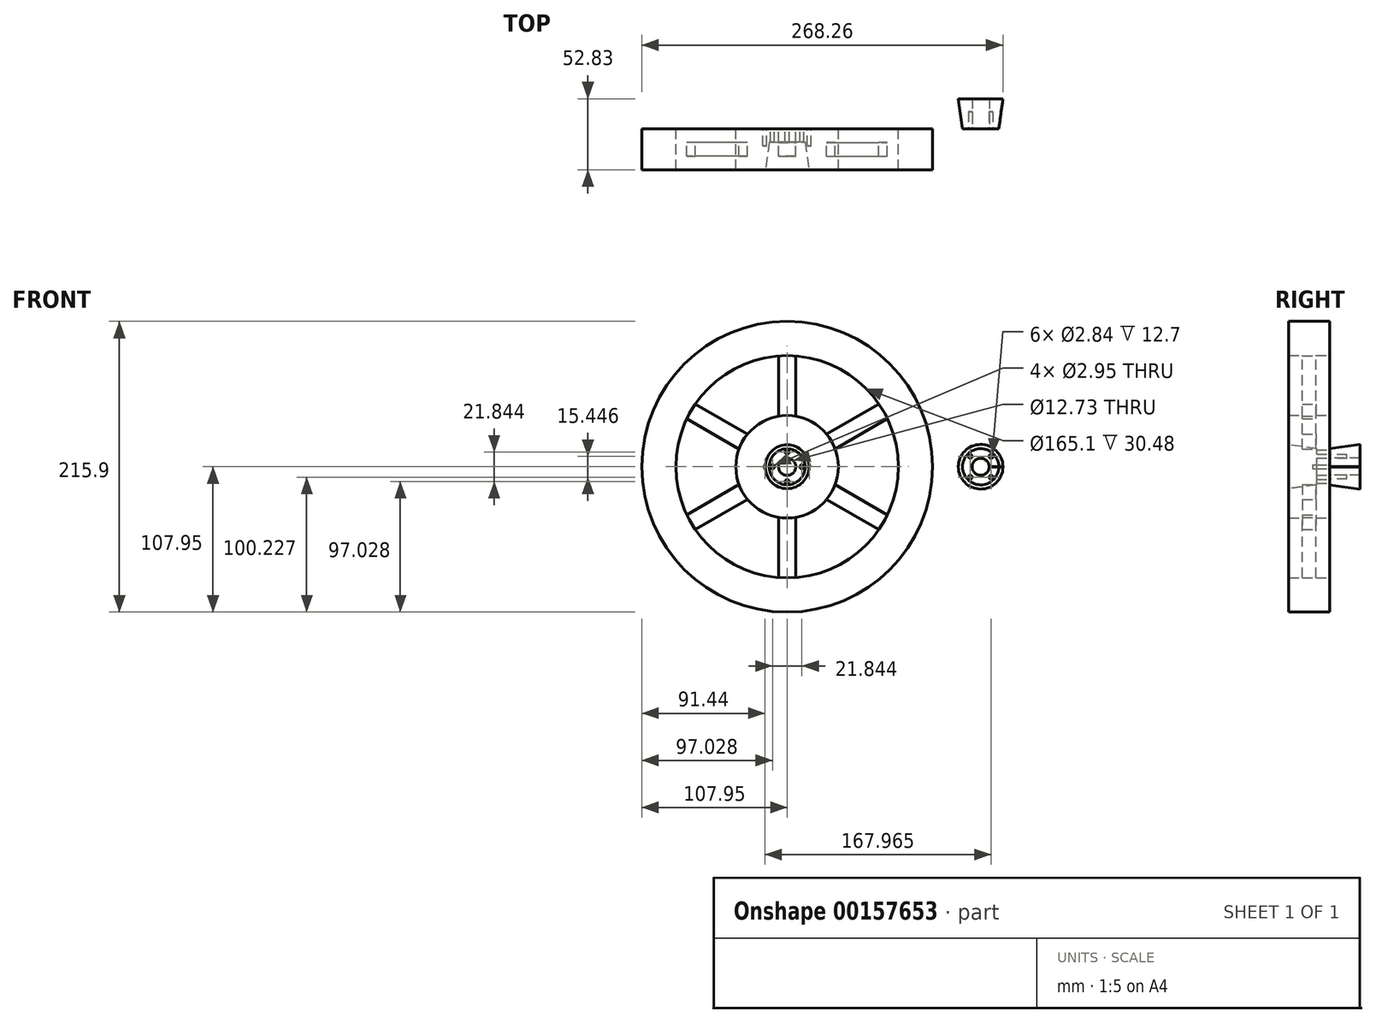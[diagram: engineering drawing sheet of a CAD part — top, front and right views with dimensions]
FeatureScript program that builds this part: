
annotation { "Feature Type Name" : "Feature", "Feature Type Description" : "" }
export const myFeature = defineFeature(function(context is Context, id is Id, definition is map)
    precondition{}
    {
        {
            var Q0;
            Q0=qCreatedBy(makeId("Front.planeOp"),FACE);
            var sketch = newSketch(context, id + "F0", { "sketchPlane" : qUnion([Q0])});
            skCircle(sketch, "E0", {"center": v(0, 0) * mm, "radius": 107.95 * mm});
            skArc(sketch, "E1", {"start": v(-74.45, 35.65) * mm, "mid": v(-82.55, 0) * mm, "end": v(-74.45, -35.65) * mm});
            skCircle(sketch, "E2", {"center": v(0, 0) * mm, "radius": 104.78 * mm});
            skArc(sketch, "E3", {"start": v(-35.7, 13.28) * mm, "mid": v(-38.1, 0) * mm, "end": v(-35.7, -13.28) * mm});
            skCircle(sketch, "E4", {"center": v(0, 0) * mm, "radius": 35.56 * mm});
            skCircle(sketch, "E5", {"center": v(0, 0) * mm, "radius": 6.36 * mm});
            skLineSegment(sketch, "E6", {"start": v(0, 0) * mm, "end": v(82.55, 0) * mm, "construction": true});
            skLineSegment(sketch, "E7", {"start": v(82.55, 0) * mm, "end": v(-82.55, 0) * mm, "construction": true});
            skLineSegment(sketch, "E8", {"start": v(0, 82.55) * mm, "end": v(0, -82.55) * mm, "construction": true});
            skLineSegment(sketch, "E9", {"start": v(-6.35, 65.1) * mm, "end": v(-6.35, 37.57) * mm});
            skLineSegment(sketch, "E10", {"start": v(-6.35, 37.57) * mm, "end": v(-6.35, 82.3) * mm});
            skLineSegment(sketch, "E11", {"start": v(6.35, 65.1) * mm, "end": v(6.35, 82.3) * mm});
            skLineSegment(sketch, "E12", {"start": v(6.35, 82.3) * mm, "end": v(6.35, 37.57) * mm});
            skLineSegment(sketch, "E13.1.0", {"start": v(-35.7, 13.28) * mm, "end": v(-74.45, 35.65) * mm});
            skLineSegment(sketch, "E13.1.1", {"start": v(-68.1, 46.65) * mm, "end": v(-29.36, 24.28) * mm});
            skLineSegment(sketch, "E13.2.0", {"start": v(-29.36, -24.28) * mm, "end": v(-68.1, -46.65) * mm});
            skLineSegment(sketch, "E13.2.1", {"start": v(-74.45, -35.65) * mm, "end": v(-35.7, -13.28) * mm});
            skLineSegment(sketch, "E13.3.0", {"start": v(6.35, -37.57) * mm, "end": v(6.35, -82.3) * mm});
            skLineSegment(sketch, "E13.3.1", {"start": v(-6.35, -82.3) * mm, "end": v(-6.35, -37.57) * mm});
            skLineSegment(sketch, "E13.4.0", {"start": v(35.7, -13.28) * mm, "end": v(74.45, -35.65) * mm});
            skLineSegment(sketch, "E13.4.1", {"start": v(68.1, -46.65) * mm, "end": v(29.36, -24.28) * mm});
            skLineSegment(sketch, "E13.5.0", {"start": v(29.36, 24.28) * mm, "end": v(68.1, 46.65) * mm});
            skLineSegment(sketch, "E13.5.1", {"start": v(74.45, 35.65) * mm, "end": v(35.7, 13.28) * mm});
            skArc(sketch, "E14.trimOffspring", {"start": v(-6.35, 82.3) * mm, "mid": v(-41.27, 71.5) * mm, "end": v(-68.1, 46.65) * mm});
            skArc(sketch, "E15.trimOffspring", {"start": v(-6.35, 37.57) * mm, "mid": v(-19.05, 33) * mm, "end": v(-29.36, 24.28) * mm});
            skArc(sketch, "E16.trimOffspring", {"start": v(68.1, 46.65) * mm, "mid": v(41.28, 71.5) * mm, "end": v(6.35, 82.3) * mm});
            skArc(sketch, "E17.trimOffspring", {"start": v(29.36, 24.28) * mm, "mid": v(19.05, 33) * mm, "end": v(6.35, 37.57) * mm});
            skArc(sketch, "E18.trimOffspring", {"start": v(74.45, -35.65) * mm, "mid": v(82.55, 0) * mm, "end": v(74.45, 35.65) * mm});
            skArc(sketch, "E19.trimOffspring", {"start": v(35.7, -13.28) * mm, "mid": v(38.1, 0) * mm, "end": v(35.7, 13.28) * mm});
            skArc(sketch, "E20.trimOffspring", {"start": v(-29.36, -24.28) * mm, "mid": v(-19.05, -33) * mm, "end": v(-6.35, -37.57) * mm});
            skArc(sketch, "E21.trimOffspring", {"start": v(-68.1, -46.65) * mm, "mid": v(-41.28, -71.5) * mm, "end": v(-6.35, -82.3) * mm});
            skArc(sketch, "E22.trimOffspring", {"start": v(6.35, -82.3) * mm, "mid": v(41.27, -71.5) * mm, "end": v(68.1, -46.65) * mm});
            skArc(sketch, "E23.trimOffspring", {"start": v(6.35, -37.57) * mm, "mid": v(19.05, -33) * mm, "end": v(29.36, -24.28) * mm});
            skSolve(sketch);
        }
        {
            var Q0;
            Q0=makeQuery(id+"F0.imprint","IMPRINT",FACE,{"disambiguationData":[TD([[makeQuery(id+"F0.imprint","IMPRINT",EDGE,{"derivedFrom":sQuery(id+"F0.wireOp",EDGE,"E1")}),-1.0]])]});
            var Q1;
            Q1=makeQuery(id+"F0.imprint","IMPRINT",FACE,{"disambiguationData":[TD([[makeQuery(id+"F0.imprint","IMPRINT",EDGE,{"derivedFrom":sQuery(id+"F0.wireOp",EDGE,"E0")}),1.0]])]});
            var Q2;
            Q2=makeQuery(id+"F0.imprint","IMPRINT",FACE,{"disambiguationData":[TD([[makeQuery(id+"F0.imprint","IMPRINT",EDGE,{"derivedFrom":sQuery(id+"F0.wireOp",EDGE,"E4")}),1.0]])]});
            extrude(context, id + "F1", {"entities" : qUnion([Q0, Q1, Q2]), "depth" : 30.48 * mm});
        }
        {
            var Q0;
            Q0=makeQuery(id+"F1.opExtrude","CAP_FACE",FACE,{"disambiguationData":[OSD([sQuery(id+"F0.wireOp",EDGE,"E0"),sQuery(id+"F0.wireOp",EDGE,"E1"),sQuery(id+"F0.wireOp",EDGE,"E3"),sQuery(id+"F0.wireOp",EDGE,"E5"),sQuery(id+"F0.wireOp",EDGE,"E10"),sQuery(id+"F0.wireOp",EDGE,"E12"),sQuery(id+"F0.wireOp",EDGE,"E13.1.0"),sQuery(id+"F0.wireOp",EDGE,"E13.1.1"),sQuery(id+"F0.wireOp",EDGE,"E13.2.0"),sQuery(id+"F0.wireOp",EDGE,"E13.2.1"),sQuery(id+"F0.wireOp",EDGE,"E13.3.0"),sQuery(id+"F0.wireOp",EDGE,"E13.3.1"),sQuery(id+"F0.wireOp",EDGE,"E13.4.0"),sQuery(id+"F0.wireOp",EDGE,"E13.4.1"),sQuery(id+"F0.wireOp",EDGE,"E13.5.0"),sQuery(id+"F0.wireOp",EDGE,"E13.5.1"),sQuery(id+"F0.wireOp",EDGE,"E14.trimOffspring"),sQuery(id+"F0.wireOp",EDGE,"E15.trimOffspring"),sQuery(id+"F0.wireOp",EDGE,"E16.trimOffspring"),sQuery(id+"F0.wireOp",EDGE,"E17.trimOffspring"),sQuery(id+"F0.wireOp",EDGE,"E18.trimOffspring"),sQuery(id+"F0.wireOp",EDGE,"E19.trimOffspring"),sQuery(id+"F0.wireOp",EDGE,"E20.trimOffspring"),sQuery(id+"F0.wireOp",EDGE,"E21.trimOffspring"),sQuery(id+"F0.wireOp",EDGE,"E22.trimOffspring"),sQuery(id+"F0.wireOp",EDGE,"E23.trimOffspring")])],"isStart":false});
            var sketch = newSketch(context, id + "F2", { "sketchPlane" : qUnion([Q0])});
            skCircle(sketch, "E24", {"center": v(0, 0) * mm, "radius": 82.55 * mm});
            skCircle(sketch, "E25", {"center": v(0, 0) * mm, "radius": 38.1 * mm});
            skSolve(sketch);
        }
        {
            var Q0;
            {var subQ2=makeQuery(id+"F1.opExtrude","CAP_EDGE",EDGE,{"disambiguationData":[OSD([sQuery(id+"F0.wireOp",EDGE,"E13.2.0")])],"isStart":false});Q0=makeQuery(id+"F2.imprint","IMPRINT",FACE,{"disambiguationData":[TD([[makeQuery(id+"F2.imprint","IMPRINT",EDGE,{"derivedFrom":subQ2}),-1.0]])]});}
            var Q1;
            {var subQ1=makeQuery(id+"F1.opExtrude","CAP_EDGE",EDGE,{"disambiguationData":[OSD([sQuery(id+"F0.wireOp",EDGE,"E13.3.0")])],"isStart":false});Q1=makeQuery(id+"F2.imprint","IMPRINT",FACE,{"disambiguationData":[TD([[makeQuery(id+"F2.imprint","IMPRINT",EDGE,{"derivedFrom":subQ1}),-1.0]])]});}
            var Q2;
            {var subQ1=makeQuery(id+"F1.opExtrude","CAP_EDGE",EDGE,{"disambiguationData":[OSD([sQuery(id+"F0.wireOp",EDGE,"E13.4.0")])],"isStart":false});Q2=makeQuery(id+"F2.imprint","IMPRINT",FACE,{"disambiguationData":[TD([[makeQuery(id+"F2.imprint","IMPRINT",EDGE,{"derivedFrom":subQ1}),-1.0]])]});}
            var Q3;
            {var subQ1=makeQuery(id+"F1.opExtrude","CAP_EDGE",EDGE,{"disambiguationData":[OSD([sQuery(id+"F0.wireOp",EDGE,"E13.5.0")])],"isStart":false});Q3=makeQuery(id+"F2.imprint","IMPRINT",FACE,{"disambiguationData":[TD([[makeQuery(id+"F2.imprint","IMPRINT",EDGE,{"derivedFrom":subQ1}),-1.0]])]});}
            var Q4;
            {var subQ1=makeQuery(id+"F1.opExtrude","CAP_EDGE",EDGE,{"disambiguationData":[OSD([sQuery(id+"F0.wireOp",EDGE,"E10")])],"isStart":false});Q4=makeQuery(id+"F2.imprint","IMPRINT",FACE,{"disambiguationData":[TD([[makeQuery(id+"F2.imprint","IMPRINT",EDGE,{"derivedFrom":subQ1}),-1.0]])]});}
            var Q5;
            {var subQ1=makeQuery(id+"F1.opExtrude","CAP_EDGE",EDGE,{"disambiguationData":[OSD([sQuery(id+"F0.wireOp",EDGE,"E13.1.0")])],"isStart":false});Q5=makeQuery(id+"F2.imprint","IMPRINT",FACE,{"disambiguationData":[TD([[makeQuery(id+"F2.imprint","IMPRINT",EDGE,{"derivedFrom":subQ1}),-1.0]])]});}
            extrude(context, id + "F3", {"entities" : qUnion([Q0, Q1, Q2, Q3, Q4, Q5]), "operationType" : NewBodyOperationType.REMOVE, "oppositeDirection" : true, "depth" : 10.16 * mm});
        }
        {
            var Q0;
            Q0=makeQuery(id+"F1.opExtrude","CAP_FACE",FACE,{"disambiguationData":[OSD([sQuery(id+"F0.wireOp",EDGE,"E0"),sQuery(id+"F0.wireOp",EDGE,"E1"),sQuery(id+"F0.wireOp",EDGE,"E3"),sQuery(id+"F0.wireOp",EDGE,"E5"),sQuery(id+"F0.wireOp",EDGE,"E10"),sQuery(id+"F0.wireOp",EDGE,"E12"),sQuery(id+"F0.wireOp",EDGE,"E13.1.0"),sQuery(id+"F0.wireOp",EDGE,"E13.1.1"),sQuery(id+"F0.wireOp",EDGE,"E13.2.0"),sQuery(id+"F0.wireOp",EDGE,"E13.2.1"),sQuery(id+"F0.wireOp",EDGE,"E13.3.0"),sQuery(id+"F0.wireOp",EDGE,"E13.3.1"),sQuery(id+"F0.wireOp",EDGE,"E13.4.0"),sQuery(id+"F0.wireOp",EDGE,"E13.4.1"),sQuery(id+"F0.wireOp",EDGE,"E13.5.0"),sQuery(id+"F0.wireOp",EDGE,"E13.5.1"),sQuery(id+"F0.wireOp",EDGE,"E14.trimOffspring"),sQuery(id+"F0.wireOp",EDGE,"E15.trimOffspring"),sQuery(id+"F0.wireOp",EDGE,"E16.trimOffspring"),sQuery(id+"F0.wireOp",EDGE,"E17.trimOffspring"),sQuery(id+"F0.wireOp",EDGE,"E18.trimOffspring"),sQuery(id+"F0.wireOp",EDGE,"E19.trimOffspring"),sQuery(id+"F0.wireOp",EDGE,"E20.trimOffspring"),sQuery(id+"F0.wireOp",EDGE,"E21.trimOffspring"),sQuery(id+"F0.wireOp",EDGE,"E22.trimOffspring"),sQuery(id+"F0.wireOp",EDGE,"E23.trimOffspring")])],"isStart":true});
            var sketch = newSketch(context, id + "F4", { "sketchPlane" : qUnion([Q0])});
            skCircle(sketch, "E26", {"center": v(0, 0) * mm, "radius": 82.55 * mm});
            skCircle(sketch, "E27", {"center": v(0, 0) * mm, "radius": 38.1 * mm});
            skSolve(sketch);
        }
        {
            var Q0;
            {var subQ2=makeQuery(id+"F1.opExtrude","CAP_EDGE",EDGE,{"disambiguationData":[OSD([sQuery(id+"F0.wireOp",EDGE,"E13.2.0")])],"isStart":true});Q0=makeQuery(id+"F4.imprint","IMPRINT",FACE,{"disambiguationData":[TD([[makeQuery(id+"F4.imprint","IMPRINT",EDGE,{"derivedFrom":subQ2}),1.0]])]});}
            var Q1;
            {var subQ1=makeQuery(id+"F1.opExtrude","CAP_EDGE",EDGE,{"disambiguationData":[OSD([sQuery(id+"F0.wireOp",EDGE,"E13.1.0")])],"isStart":true});Q1=makeQuery(id+"F4.imprint","IMPRINT",FACE,{"disambiguationData":[TD([[makeQuery(id+"F4.imprint","IMPRINT",EDGE,{"derivedFrom":subQ1}),1.0]])]});}
            var Q2;
            {var subQ1=makeQuery(id+"F1.opExtrude","CAP_EDGE",EDGE,{"disambiguationData":[OSD([sQuery(id+"F0.wireOp",EDGE,"E10")])],"isStart":true});Q2=makeQuery(id+"F4.imprint","IMPRINT",FACE,{"disambiguationData":[TD([[makeQuery(id+"F4.imprint","IMPRINT",EDGE,{"derivedFrom":subQ1}),1.0]])]});}
            var Q3;
            {var subQ1=makeQuery(id+"F1.opExtrude","CAP_EDGE",EDGE,{"disambiguationData":[OSD([sQuery(id+"F0.wireOp",EDGE,"E13.5.0")])],"isStart":true});Q3=makeQuery(id+"F4.imprint","IMPRINT",FACE,{"disambiguationData":[TD([[makeQuery(id+"F4.imprint","IMPRINT",EDGE,{"derivedFrom":subQ1}),1.0]])]});}
            var Q4;
            {var subQ1=makeQuery(id+"F1.opExtrude","CAP_EDGE",EDGE,{"disambiguationData":[OSD([sQuery(id+"F0.wireOp",EDGE,"E13.4.0")])],"isStart":true});Q4=makeQuery(id+"F4.imprint","IMPRINT",FACE,{"disambiguationData":[TD([[makeQuery(id+"F4.imprint","IMPRINT",EDGE,{"derivedFrom":subQ1}),1.0]])]});}
            var Q5;
            {var subQ1=makeQuery(id+"F1.opExtrude","CAP_EDGE",EDGE,{"disambiguationData":[OSD([sQuery(id+"F0.wireOp",EDGE,"E13.3.0")])],"isStart":true});Q5=makeQuery(id+"F4.imprint","IMPRINT",FACE,{"disambiguationData":[TD([[makeQuery(id+"F4.imprint","IMPRINT",EDGE,{"derivedFrom":subQ1}),1.0]])]});}
            extrude(context, id + "F5", {"entities" : qUnion([Q0, Q1, Q2, Q3, Q4, Q5]), "operationType" : NewBodyOperationType.REMOVE, "oppositeDirection" : true, "depth" : 10.16 * mm});
        }
        {
            var Q0;
            {var subQ1=sQuery(id+"F0.wireOp",EDGE,"E13.5.0");var subQ2=sQuery(id+"F0.wireOp",EDGE,"E13.5.1");var subQ3=sQuery(id+"F0.wireOp",EDGE,"E23.trimOffspring");var subQ4=sQuery(id+"F0.wireOp",EDGE,"E19.trimOffspring");var subQ5=sQuery(id+"F0.wireOp",EDGE,"E20.trimOffspring");var subQ6=sQuery(id+"F0.wireOp",EDGE,"E3");var subQ7=sQuery(id+"F0.wireOp",EDGE,"E13.1.0");var subQ8=sQuery(id+"F0.wireOp",EDGE,"E13.1.1");var subQ9=sQuery(id+"F0.wireOp",EDGE,"E17.trimOffspring");var subQ10=sQuery(id+"F0.wireOp",EDGE,"E5");var subQ11=sQuery(id+"F0.wireOp",EDGE,"E15.trimOffspring");var subQ12=sQuery(id+"F0.wireOp",EDGE,"E10");var subQ13=sQuery(id+"F0.wireOp",EDGE,"E12");var subQ14=sQuery(id+"F0.wireOp",EDGE,"E13.2.1");var subQ15=sQuery(id+"F0.wireOp",EDGE,"E13.2.0");var subQ16=sQuery(id+"F0.wireOp",EDGE,"E13.3.0");var subQ17=sQuery(id+"F0.wireOp",EDGE,"E13.3.1");var subQ18=sQuery(id+"F0.wireOp",EDGE,"E13.4.0");var subQ19=sQuery(id+"F0.wireOp",EDGE,"E13.4.1");Q0=makeQuery(id+"F3.boolean.opBoolean","SPLIT",FACE,{"disambiguationData":[TD([makeQuery(id+"F1.opExtrude","SWEPT_FACE",FACE,{"disambiguationData":[OSD([subQ6])]})])],"derivedFrom":makeQuery(id+"F1.opExtrude","CAP_FACE",FACE,{"disambiguationData":[OSD([sQuery(id+"F0.wireOp",EDGE,"E0"),sQuery(id+"F0.wireOp",EDGE,"E1"),subQ6,subQ10,subQ12,subQ13,subQ7,subQ8,subQ15,subQ14,subQ16,subQ17,subQ18,subQ19,subQ1,subQ2,sQuery(id+"F0.wireOp",EDGE,"E14.trimOffspring"),subQ11,sQuery(id+"F0.wireOp",EDGE,"E16.trimOffspring"),subQ9,sQuery(id+"F0.wireOp",EDGE,"E18.trimOffspring"),subQ4,subQ5,sQuery(id+"F0.wireOp",EDGE,"E21.trimOffspring"),sQuery(id+"F0.wireOp",EDGE,"E22.trimOffspring"),subQ3])],"isStart":false})});}
            var sketch = newSketch(context, id + "F6", { "sketchPlane" : qUnion([Q0])});
            skCircle(sketch, "E28", {"center": v(0, 0) * mm, "radius": 13.34 * mm});
            skSolve(sketch);
        }
        {
            var Q0;
            Q0=makeQuery(id+"F6.imprint","IMPRINT",FACE,{"disambiguationData":[TD([[makeQuery(id+"F6.imprint","IMPRINT",EDGE,{"derivedFrom":sQuery(id+"F6.wireOp",EDGE,"E28")}),1.0]])]});
            extrude(context, id + "F7", {"entities" : qUnion([Q0]), "operationType" : NewBodyOperationType.REMOVE, "oppositeDirection" : true, "depth" : 20.83 * mm});
        }
        {
            var Q0;
            Q0=makeQuery(id+"F7.boolean.opBoolean","COPY",FACE,{"derivedFrom":makeQuery(id+"F7.opExtrude","CAP_FACE",FACE,{"disambiguationData":[OSD([sQuery(id+"F0.wireOp",EDGE,"E5"),sQuery(id+"F6.wireOp",EDGE,"E28")])],"isStart":false})});
            extrude(context, id + "F8", {"entities" : qUnion([Q0]), "operationType" : NewBodyOperationType.REMOVE, "depth" : 25.4 * mm, "hasDraft" : true, "draftAngle" : 8 * degree});
        }
        {
            var Q0;
            {var subQ1=sQuery(id+"F0.wireOp",EDGE,"E13.5.0");var subQ2=sQuery(id+"F0.wireOp",EDGE,"E13.5.1");var subQ3=sQuery(id+"F0.wireOp",EDGE,"E23.trimOffspring");var subQ4=sQuery(id+"F0.wireOp",EDGE,"E19.trimOffspring");var subQ5=sQuery(id+"F0.wireOp",EDGE,"E20.trimOffspring");var subQ7=sQuery(id+"F0.wireOp",EDGE,"E13.1.0");var subQ8=sQuery(id+"F0.wireOp",EDGE,"E13.1.1");var subQ9=sQuery(id+"F0.wireOp",EDGE,"E3");var subQ10=sQuery(id+"F0.wireOp",EDGE,"E17.trimOffspring");var subQ11=sQuery(id+"F0.wireOp",EDGE,"E5");var subQ12=sQuery(id+"F0.wireOp",EDGE,"E10");var subQ13=sQuery(id+"F0.wireOp",EDGE,"E12");var subQ14=sQuery(id+"F0.wireOp",EDGE,"E15.trimOffspring");var subQ15=sQuery(id+"F0.wireOp",EDGE,"E13.2.1");var subQ16=sQuery(id+"F0.wireOp",EDGE,"E13.2.0");var subQ17=sQuery(id+"F0.wireOp",EDGE,"E13.4.0");var subQ18=sQuery(id+"F0.wireOp",EDGE,"E13.4.1");var subQ19=sQuery(id+"F0.wireOp",EDGE,"E13.3.0");var subQ20=sQuery(id+"F0.wireOp",EDGE,"E13.3.1");Q0=makeQuery(id+"F5.boolean.opBoolean","SPLIT",FACE,{"disambiguationData":[TD([makeQuery(id+"F1.opExtrude","SWEPT_FACE",FACE,{"disambiguationData":[OSD([subQ9])]})])],"derivedFrom":makeQuery(id+"F1.opExtrude","CAP_FACE",FACE,{"disambiguationData":[OSD([sQuery(id+"F0.wireOp",EDGE,"E0"),sQuery(id+"F0.wireOp",EDGE,"E1"),subQ9,subQ11,subQ12,subQ13,subQ7,subQ8,subQ16,subQ15,subQ19,subQ20,subQ17,subQ18,subQ1,subQ2,sQuery(id+"F0.wireOp",EDGE,"E14.trimOffspring"),subQ14,sQuery(id+"F0.wireOp",EDGE,"E16.trimOffspring"),subQ10,sQuery(id+"F0.wireOp",EDGE,"E18.trimOffspring"),subQ4,subQ5,sQuery(id+"F0.wireOp",EDGE,"E21.trimOffspring"),sQuery(id+"F0.wireOp",EDGE,"E22.trimOffspring"),subQ3])],"isStart":true})});}
            var sketch = newSketch(context, id + "F9", { "sketchPlane" : qUnion([Q0])});
            skCircle(sketch, "E29", {"center": v(0, 0) * mm, "radius": 10.92 * mm, "construction": true});
            skCircle(sketch, "E30", {"center": v(0, 10.92) * mm, "radius": 1.47 * mm});
            skCircle(sketch, "E31.1.0", {"center": v(-10.92, 0) * mm, "radius": 1.47 * mm});
            skCircle(sketch, "E31.2.0", {"center": v(0, -10.92) * mm, "radius": 1.47 * mm});
            skCircle(sketch, "E31.3.0", {"center": v(10.92, 0) * mm, "radius": 1.47 * mm});
            skSolve(sketch);
        }
        {
            var Q0;
            Q0=makeQuery(id+"F9.imprint","IMPRINT",FACE,{"disambiguationData":[TD([[makeQuery(id+"F9.imprint","IMPRINT",EDGE,{"derivedFrom":sQuery(id+"F9.wireOp",EDGE,"E31.1.0")}),1.0]])]});
            var Q1;
            Q1=makeQuery(id+"F9.imprint","IMPRINT",FACE,{"disambiguationData":[TD([[makeQuery(id+"F9.imprint","IMPRINT",EDGE,{"derivedFrom":sQuery(id+"F9.wireOp",EDGE,"E30")}),1.0]])]});
            var Q2;
            Q2=makeQuery(id+"F9.imprint","IMPRINT",FACE,{"disambiguationData":[TD([[makeQuery(id+"F9.imprint","IMPRINT",EDGE,{"derivedFrom":sQuery(id+"F9.wireOp",EDGE,"E31.2.0")}),1.0]])]});
            var Q3;
            Q3=makeQuery(id+"F9.imprint","IMPRINT",FACE,{"disambiguationData":[TD([[makeQuery(id+"F9.imprint","IMPRINT",EDGE,{"derivedFrom":sQuery(id+"F9.wireOp",EDGE,"E31.3.0")}),1.0]])]});
            extrude(context, id + "F10", {"entities" : qUnion([Q0, Q1, Q2, Q3]), "operationType" : NewBodyOperationType.REMOVE, "oppositeDirection" : true, "depth" : 25.4 * mm});
        }
        {
            var Q0;
            {var subQ1=sQuery(id+"F0.wireOp",EDGE,"E13.5.0");var subQ2=sQuery(id+"F0.wireOp",EDGE,"E13.5.1");var subQ3=sQuery(id+"F0.wireOp",EDGE,"E23.trimOffspring");var subQ4=sQuery(id+"F0.wireOp",EDGE,"E19.trimOffspring");var subQ5=sQuery(id+"F0.wireOp",EDGE,"E20.trimOffspring");var subQ7=sQuery(id+"F0.wireOp",EDGE,"E13.1.0");var subQ8=sQuery(id+"F0.wireOp",EDGE,"E13.1.1");var subQ9=sQuery(id+"F0.wireOp",EDGE,"E3");var subQ10=sQuery(id+"F0.wireOp",EDGE,"E17.trimOffspring");var subQ11=sQuery(id+"F0.wireOp",EDGE,"E5");var subQ12=sQuery(id+"F0.wireOp",EDGE,"E10");var subQ13=sQuery(id+"F0.wireOp",EDGE,"E12");var subQ14=sQuery(id+"F0.wireOp",EDGE,"E15.trimOffspring");var subQ15=sQuery(id+"F0.wireOp",EDGE,"E13.2.1");var subQ16=sQuery(id+"F0.wireOp",EDGE,"E13.2.0");var subQ17=sQuery(id+"F0.wireOp",EDGE,"E13.4.0");var subQ18=sQuery(id+"F0.wireOp",EDGE,"E13.4.1");var subQ19=sQuery(id+"F0.wireOp",EDGE,"E13.3.0");var subQ20=sQuery(id+"F0.wireOp",EDGE,"E13.3.1");Q0=makeQuery(id+"F5.boolean.opBoolean","SPLIT",FACE,{"disambiguationData":[TD([makeQuery(id+"F1.opExtrude","SWEPT_FACE",FACE,{"disambiguationData":[OSD([subQ9])]})])],"derivedFrom":makeQuery(id+"F1.opExtrude","CAP_FACE",FACE,{"disambiguationData":[OSD([sQuery(id+"F0.wireOp",EDGE,"E0"),sQuery(id+"F0.wireOp",EDGE,"E1"),subQ9,subQ11,subQ12,subQ13,subQ7,subQ8,subQ16,subQ15,subQ19,subQ20,subQ17,subQ18,subQ1,subQ2,sQuery(id+"F0.wireOp",EDGE,"E14.trimOffspring"),subQ14,sQuery(id+"F0.wireOp",EDGE,"E16.trimOffspring"),subQ10,sQuery(id+"F0.wireOp",EDGE,"E18.trimOffspring"),subQ4,subQ5,sQuery(id+"F0.wireOp",EDGE,"E21.trimOffspring"),sQuery(id+"F0.wireOp",EDGE,"E22.trimOffspring"),subQ3])],"isStart":true})});}
            var sketch = newSketch(context, id + "F11", { "sketchPlane" : qUnion([Q0])});
            skCircle(sketch, "E32", {"center": v(0, 0) * mm, "radius": 16.51 * mm, "construction": true});
            skCircle(sketch, "E33", {"center": v(16.51, 0) * mm, "radius": 1.42 * mm});
            skCircle(sketch, "E34", {"center": v(-16.51, 0) * mm, "radius": 1.42 * mm});
            skSolve(sketch);
        }
        {
            var Q0;
            Q0=makeQuery(id+"F11.imprint","IMPRINT",FACE,{"disambiguationData":[TD([[makeQuery(id+"F11.imprint","IMPRINT",EDGE,{"derivedFrom":sQuery(id+"F11.wireOp",EDGE,"E34")}),1.0]])]});
            var Q1;
            Q1=makeQuery(id+"F11.imprint","IMPRINT",FACE,{"disambiguationData":[TD([[makeQuery(id+"F11.imprint","IMPRINT",EDGE,{"derivedFrom":sQuery(id+"F11.wireOp",EDGE,"E33")}),1.0]])]});
            extrude(context, id + "F12", {"entities" : qUnion([Q0, Q1]), "operationType" : NewBodyOperationType.REMOVE, "oppositeDirection" : true, "depth" : 12.7 * mm});
        }
        {
            var Q0;
            Q0=qCreatedBy(makeId("Front.planeOp"),FACE);
            var sketch = newSketch(context, id + "F13", { "sketchPlane" : qUnion([Q0])});
            skCircle(sketch, "E35", {"center": v(143.73, 0) * mm, "radius": 13.44 * mm});
            skLineSegment(sketch, "E36", {"start": v(143.73, 0) * mm, "end": v(130.3, 0) * mm, "construction": true});
            skLineSegment(sketch, "E37", {"start": v(143.73, 0) * mm, "end": v(134.23, 9.5) * mm, "construction": true});
            skCircle(sketch, "E38", {"center": v(143.73, 0) * mm, "radius": 10.92 * mm, "construction": true});
            skCircle(sketch, "E39", {"center": v(136, 7.72) * mm, "radius": 1.42 * mm});
            skCircle(sketch, "E40.1.0", {"center": v(136, -7.72) * mm, "radius": 1.42 * mm});
            skCircle(sketch, "E40.2.0", {"center": v(151.46, -7.72) * mm, "radius": 1.42 * mm});
            skCircle(sketch, "E40.3.0", {"center": v(151.46, 7.72) * mm, "radius": 1.42 * mm});
            skCircle(sketch, "E41", {"center": v(143.73, 0) * mm, "radius": 6.35 * mm});
            skSolve(sketch);
        }
        {
            var Q0;
            Q0=makeQuery(id+"F13.imprint","IMPRINT",FACE,{"disambiguationData":[TD([[makeQuery(id+"F13.imprint","IMPRINT",EDGE,{"derivedFrom":sQuery(id+"F13.wireOp",EDGE,"E35")}),1.0]])]});
            var Q1;
            Q1=makeQuery(id+"F13.imprint","IMPRINT",FACE,{"disambiguationData":[TD([[makeQuery(id+"F13.imprint","IMPRINT",EDGE,{"derivedFrom":sQuery(id+"F13.wireOp",EDGE,"E39")}),1.0]])]});
            var Q2;
            Q2=makeQuery(id+"F13.imprint","IMPRINT",FACE,{"disambiguationData":[TD([[makeQuery(id+"F13.imprint","IMPRINT",EDGE,{"derivedFrom":sQuery(id+"F13.wireOp",EDGE,"E40.1.0")}),1.0]])]});
            var Q3;
            Q3=makeQuery(id+"F13.imprint","IMPRINT",FACE,{"disambiguationData":[TD([[makeQuery(id+"F13.imprint","IMPRINT",EDGE,{"derivedFrom":sQuery(id+"F13.wireOp",EDGE,"E40.2.0")}),1.0]])]});
            var Q4;
            Q4=makeQuery(id+"F13.imprint","IMPRINT",FACE,{"disambiguationData":[TD([[makeQuery(id+"F13.imprint","IMPRINT",EDGE,{"derivedFrom":sQuery(id+"F13.wireOp",EDGE,"E40.3.0")}),1.0]])]});
            var Q5;
            Q5=makeQuery(id+"F13.imprint","IMPRINT",FACE,{"disambiguationData":[TD([[makeQuery(id+"F13.imprint","IMPRINT",EDGE,{"derivedFrom":sQuery(id+"F13.wireOp",EDGE,"E41")}),1.0]])]});
            extrude(context, id + "F14", {"entities" : qUnion([Q0, Q1, Q2, Q3, Q4, Q5]), "oppositeDirection" : true, "depth" : 22.35 * mm, "hasDraft" : true, "draftAngle" : 8 * degree});
        }
        {
            var Q0;
            Q0=makeQuery(id+"F13.imprint","IMPRINT",FACE,{"disambiguationData":[TD([[makeQuery(id+"F13.imprint","IMPRINT",EDGE,{"derivedFrom":sQuery(id+"F13.wireOp",EDGE,"E39")}),1.0]])]});
            var Q1;
            Q1=makeQuery(id+"F13.imprint","IMPRINT",FACE,{"disambiguationData":[TD([[makeQuery(id+"F13.imprint","IMPRINT",EDGE,{"derivedFrom":sQuery(id+"F13.wireOp",EDGE,"E40.3.0")}),1.0]])]});
            var Q2;
            Q2=makeQuery(id+"F13.imprint","IMPRINT",FACE,{"disambiguationData":[TD([[makeQuery(id+"F13.imprint","IMPRINT",EDGE,{"derivedFrom":sQuery(id+"F13.wireOp",EDGE,"E40.2.0")}),1.0]])]});
            var Q3;
            Q3=makeQuery(id+"F13.imprint","IMPRINT",FACE,{"disambiguationData":[TD([[makeQuery(id+"F13.imprint","IMPRINT",EDGE,{"derivedFrom":sQuery(id+"F13.wireOp",EDGE,"E40.1.0")}),1.0]])]});
            extrude(context, id + "F15", {"entities" : qUnion([Q0, Q1, Q2, Q3]), "operationType" : NewBodyOperationType.REMOVE, "oppositeDirection" : true, "depth" : 12.7 * mm});
        }
        {
            var Q0;
            Q0=makeQuery(id+"F13.imprint","IMPRINT",FACE,{"disambiguationData":[TD([[makeQuery(id+"F13.imprint","IMPRINT",EDGE,{"derivedFrom":sQuery(id+"F13.wireOp",EDGE,"E41")}),1.0]])]});
            extrude(context, id + "F16", {"entities" : qUnion([Q0]), "operationType" : NewBodyOperationType.REMOVE, "oppositeDirection" : true, "depth" : 25.4 * mm});
        }
        {
            var Q0;
            Q0=makeQuery(id+"F13.imprint","IMPRINT",FACE,{"disambiguationData":[TD([[makeQuery(id+"F13.imprint","IMPRINT",EDGE,{"derivedFrom":sQuery(id+"F13.wireOp",EDGE,"E35")}),1.0]])]});
            var sketch = newSketch(context, id + "F17", { "sketchPlane" : qUnion([Q0])});
            skLineSegment(sketch, "E42", {"start": v(144.11, 0) * mm, "end": v(164.89, 0) * mm, "construction": true});
            skLineSegment(sketch, "E43.bottom", {"start": v(162.78, 0.25) * mm, "end": v(145, 0.25) * mm});
            skLineSegment(sketch, "E43.top", {"start": v(162.78, -0.25) * mm, "end": v(145, -0.25) * mm});
            skLineSegment(sketch, "E43.left", {"start": v(162.78, 0.25) * mm, "end": v(162.78, -0.25) * mm});
            skLineSegment(sketch, "E43.right", {"start": v(145, 0.25) * mm, "end": v(145, -0.25) * mm});
            skPoint(sketch, "E43.middle", {"position": v(153.89, 0) * mm});
            skSolve(sketch);
        }
        {
            var Q0;
            {var subQ0=sQuery(id+"F17.wireOp",EDGE,"E43.bottom");var subQ1=makeQuery(id+"F13.imprint","IMPRINT",EDGE,{"derivedFrom":sQuery(id+"F13.wireOp",EDGE,"E35")});var subQ2=makeQuery(id+"F17.imprint","INTERSECT",VERTEX,{"derivedFrom":[subQ1,subQ0]});Q0=makeQuery(id+"F17.imprint","IMPRINT",FACE,{"disambiguationData":[TD([[makeQuery(id+"F17.imprint","IMPRINT",EDGE,{"disambiguationData":[TD([[subQ2,-1.0]])],"derivedFrom":subQ0}),1.0]])]});}
            var Q1;
            {var subQ0=sQuery(id+"F17.wireOp",EDGE,"E43.left");Q1=makeQuery(id+"F17.imprint","IMPRINT",FACE,{"disambiguationData":[TD([[makeQuery(id+"F17.imprint","IMPRINT",EDGE,{"derivedFrom":subQ0}),-1.0]])]});}
            extrude(context, id + "F18", {"entities" : qUnion([Q0, Q1]), "operationType" : NewBodyOperationType.REMOVE, "oppositeDirection" : true, "depth" : 25.4 * mm});
        }
    });
